# Revit family: Hager-UNIVERS-Surface_mounted-IP30-With_Cover-With_DIN-Hosted-AT-de
name_source: partatom
category: Electrical Equipment
units: mm (PartAtom-declared; Revit-internal decimal feet)

## family parameters
Cut with Voids When Loaded = No
Host = Face
Maintain Annotation Orientation = Yes
Panel Configuration = Two Columns, Circuits Across
Part Type = Panelboard
Room Calculation Point = No
Round Connector Dimension = Use Diameter
Shared = No

## types (4) — shared parameters
BC_MODEL_ID = 1554443
BC_OBJECT_ID = 513923
BC_OBJECT_VERSION = #3
Code hager = ADD-EC000214_EU
EF000008 - Breite = 550 mm  [stored 1.80446 ft]
EF000024 - UV-beständig = No
EF000049 - Tiefe = 161 mm  [stored 0.528215 ft]
EF000116 - RAL-Nummer = 9010
EF001062 - EMV-Ausführung = No
EF001088 - Anbaumöglichkeit = Yes
EF001134 - DIN-Schiene = Yes
EF005474 - Schutzart (IP) = IP30
EF006244 - Transparenter Deckel/Tür = No
EF006306 - Mit Schloss = No
ETIM class code = EC000214
ETIM class name = Small distribution board
HG000002-Mit tür = Yes
HG000003-Bereich = UNIVERS
HG000005-Dicke = 2 mm  [stored 0.00656168 ft]
HG000006-Unterputz = No
HG000009-Doppelflügeligen Tür = No
HG000010-Asymmetrische Türen = No
HG000012-Türschwenkwinkel = 90.00°
HG000013-Tür links = No
HG000014-Tür rechts = Yes
HG000015-Sichtbarkeit der Türöffnung = Yes
HG000016-3D-Türsichtbarkeit = Yes
HG000017-Distanz zwischen den Polen = 18 mm  [stored 0.0590551 ft]
HG000060-RAL-number = 9010
HG000099-Onfly Template ID-de-AT = 507532
Manufacturer = Hager
Name = UNIVERS-Surface_mounted-IP30-With_Cover-With_DIN-AT
Name BIM&CO = Electricity
Name hager = ADD_Enclosures_EC000214
Uniformat = Low Tension Service & Dist.
Uniformat code = D501001
zero-valued in all types: Default Elevation, EF000218 - Einbautiefe, EF001131 - Innentiefe

## per-type parameters (varying)
| type | BC_VARIANT_ID | EF000003 - Montageart | EF000007 - Farbe | EF000040 - Höhe | EF000118 - Mit Montageplatte | EF000266 - Anzahl der Reihen | EF000332 - Einbauhöhe | EF000846 - Einbaubreite | EF002950 - Breite in Teilungseinheiten | EF004462 - Art der Schließung | EF009212 - Ausführung Deckel | EF015776 - Erdungsklemmenblock | EF015777 - Neutralleiterklemmenblock | EF015941 - Signaldurchlassende Tür | HG000001-Anzahl der Spalten | HG000004-Herstellerreferenz | HG000007-Anzahl der leeren Spalten | HG000008-Anzahl der leeren Reihen | HG000011-Leere Reihen von unten | HGEF000266-Anzahl der Reihen | HGEF0002950-Breite in Teilungseinheiten |
| UNIVERS-Surface_mounted_W550_H650_D161_12_Modular_Spacing-FWQ42K3 | 1179126 | Aufputz/Unterputz | weiß | 650 mm  [stored 2.13255 ft] | Yes | 4 | 650 mm  [stored 2.13255 ft] | 550 mm  [stored 1.80446 ft] | 12 | sonstige | mit Ausschnitt | Yes | Yes | Yes | 1 | FWQ42K3 | 1 | 0 | No | 4 | 12 |
| UNIVERS-Surface_mounted_W550_H800_D161_12_Modular_Spacing-FWQ52K3 | 1179127 | Aufputz/Unterputz | weiß | 800 mm  [stored 2.62467 ft] | Yes | 5 | 800 mm  [stored 2.62467 ft] | 550 mm  [stored 1.80446 ft] | 12 | sonstige | mit Ausschnitt | Yes | Yes | No | 1 | FWQ52K3 | 1 | 0 | No | 5 | 12 |
| UNIVERS-Surface_mounted_W550_H800_D161_24_Modular_Spacing-FWQ52M5 | 1179128 | Aufputz |  | 800 mm  [stored 2.62467 ft] | No | 5 | 0 mm  [stored 0 ft] | 0 mm  [stored 0 ft] | 24 |  |  | No | No | No | 1 | FWQ52M5 | 0 | 2 | Yes | 5 | 24 |
| UNIVERS-Surface_mounted_W550_H950_D161_12_Modular_Spacing-FWQ62K3 | 1179129 | Aufputz/Unterputz | weiß | 950 mm  [stored 3.1168 ft] | Yes | 6 | 950 mm  [stored 3.1168 ft] | 550 mm  [stored 1.80446 ft] | 12 | sonstige | mit Ausschnitt | Yes | Yes | No | 2 | FWQ62K3 | 1 | 0 | No | 6 | 12 |

note: column(s) folded — value = type name in every type: Reference

note: [stored X ft] marks values corroborated as IEEE doubles in the binary element streams (Revit-internal decimal feet)

## geometry (parser evidence)
native form markers: Sweep x17
no freeform markers — native parametric forms only
